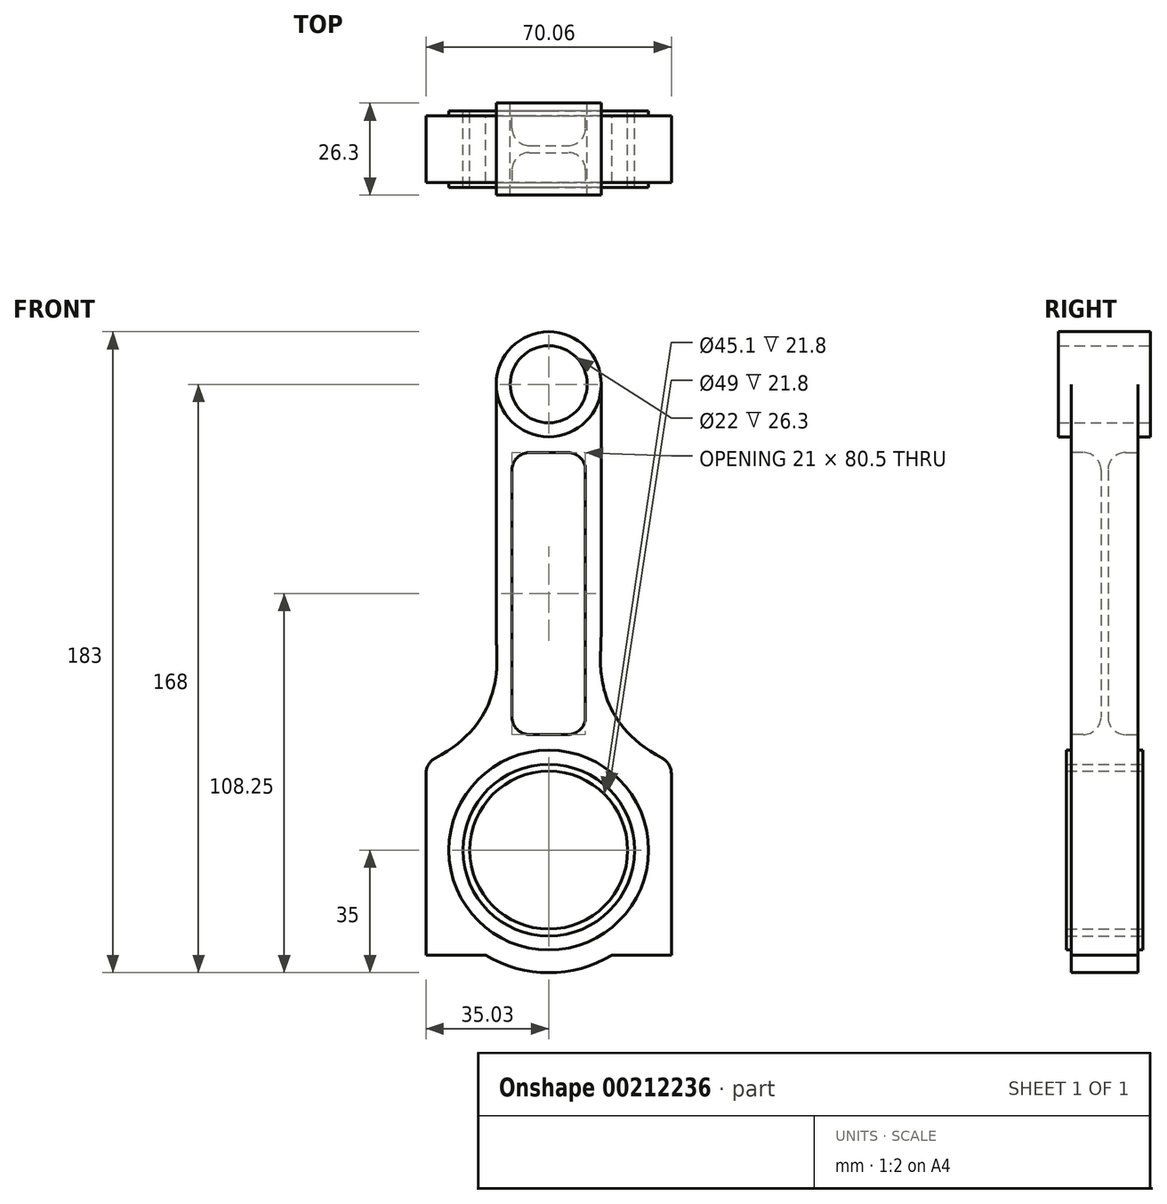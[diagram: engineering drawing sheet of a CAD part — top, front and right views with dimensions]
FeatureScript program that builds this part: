
annotation { "Feature Type Name" : "Feature", "Feature Type Description" : "" }
export const myFeature = defineFeature(function(context is Context, id is Id, definition is map)
    precondition{}
    {
        {
            var Q0;
            Q0=qCreatedBy(makeId("Front.planeOp"),FACE);
            var sketch = newSketch(context, id + "F0", { "sketchPlane" : qUnion([Q0])});
            skCircle(sketch, "E0", {"center": v(0, 0) * mm, "radius": 24.5 * mm});
            skCircle(sketch, "E1", {"center": v(0, 0) * mm, "radius": 22.55 * mm});
            skCircle(sketch, "E2", {"center": v(0, 133) * mm, "radius": 11 * mm});
            skCircle(sketch, "E3", {"center": v(0, 0) * mm, "radius": 28.5 * mm});
            skCircle(sketch, "E4", {"center": v(0, 133) * mm, "radius": 15 * mm});
            skLineSegment(sketch, "E5", {"start": v(0, 172.33) * mm, "end": v(0, -46.15) * mm, "construction": true});
            skCircle(sketch, "E6", {"center": v(0, 0) * mm, "radius": 35 * mm});
            skLineSegment(sketch, "E7", {"start": v(55.37, 133) * mm, "end": v(-76.38, 133) * mm, "construction": true});
            skLineSegment(sketch, "E8", {"start": v(-15, 133) * mm, "end": v(-15, 31.62) * mm});
            skLineSegment(sketch, "E9.MirrorCS", {"start": v(15, 133) * mm, "end": v(15, 31.62) * mm});
            skFitSpline(sketch, "E10", {"points": [v(-15, 65) * mm, v(-15, 50.33) * mm, v(-35.03, 25) * mm], "startDerivative": vector(0, -61.56) * mm, "endDerivative": vector(-82.01, -36.74) * mm});
            skLineSegment(sketch, "E11", {"start": v(-35.03, 25) * mm, "end": v(-35.03, -30) * mm});
            skLineSegment(sketch, "E12", {"start": v(-35.03, -30) * mm, "end": v(-18.03, -30) * mm});
            skFitSpline(sketch, "E13.MirrorCS", {"points": [v(15, 65) * mm, v(15, 50.33) * mm, v(35.03, 25) * mm], "startDerivative": vector(0, -61.56) * mm, "endDerivative": vector(82.01, -36.74) * mm});
            skLineSegment(sketch, "E14.MirrorCS", {"start": v(35.03, 25) * mm, "end": v(35.03, -30) * mm});
            skLineSegment(sketch, "E15.MirrorCS", {"start": v(35.03, -30) * mm, "end": v(18.03, -30) * mm});
            skSolve(sketch);
        }
        {
            var Q0;
            {var subQ0=sQuery(id+"F0.wireOp",EDGE,"E10");Q0=makeQuery(id+"F0.imprint","IMPRINT",FACE,{"disambiguationData":[TD([[makeQuery(id+"F0.imprint","IMPRINT",EDGE,{"derivedFrom":subQ0}),1.0]])]});}
            var Q1;
            {var subQ0=sQuery(id+"F0.wireOp",EDGE,"E13.MirrorCS");Q1=makeQuery(id+"F0.imprint","IMPRINT",FACE,{"disambiguationData":[TD([[makeQuery(id+"F0.imprint","IMPRINT",EDGE,{"derivedFrom":subQ0}),-1.0]])]});}
            var Q2;
            Q2=makeQuery(id+"F0.imprint","IMPRINT",FACE,{"disambiguationData":[TD([[makeQuery(id+"F0.imprint","IMPRINT",EDGE,{"derivedFrom":sQuery(id+"F0.wireOp",EDGE,"E3")}),-1.0]])]});
            var Q3;
            {var subQ0=sQuery(id+"F0.wireOp",EDGE,"E8");var subQ4=sQuery(id+"F0.wireOp",EDGE,"E4");var subQ5=makeQuery(id+"F0.imprint","INTERSECT",VERTEX,{"derivedFrom":[subQ4,subQ0]});Q3=makeQuery(id+"F0.imprint","IMPRINT",FACE,{"disambiguationData":[TD([[makeQuery(id+"F0.imprint","IMPRINT",EDGE,{"disambiguationData":[TD([[subQ5,-1.0]])],"derivedFrom":subQ4}),-1.0]])]});}
            extrude(context, id + "F1", {"entities" : qUnion([Q0, Q1, Q2, Q3]), "endBound" : BoundingType.SYMMETRIC, "depth" : 19 * mm});
        }
        {
            var Q0;
            Q0=makeQuery(id+"F0.imprint","IMPRINT",FACE,{"disambiguationData":[TD([[makeQuery(id+"F0.imprint","IMPRINT",EDGE,{"derivedFrom":sQuery(id+"F0.wireOp",EDGE,"E0")}),-1.0]])]});
            extrude(context, id + "F2", {"entities" : qUnion([Q0]), "operationType" : NewBodyOperationType.ADD, "endBound" : BoundingType.SYMMETRIC, "depth" : 21.8 * mm});
        }
        {
            var Q0;
            Q0=makeQuery(id+"F0.imprint","IMPRINT",FACE,{"disambiguationData":[TD([[makeQuery(id+"F0.imprint","IMPRINT",EDGE,{"derivedFrom":sQuery(id+"F0.wireOp",EDGE,"E2")}),-1.0]])]});
            extrude(context, id + "F3", {"entities" : qUnion([Q0]), "operationType" : NewBodyOperationType.ADD, "endBound" : BoundingType.SYMMETRIC, "depth" : 26.3 * mm});
        }
        {
            var Q0;
            Q0=makeQuery(id+"F0.imprint","IMPRINT",FACE,{"disambiguationData":[TD([[makeQuery(id+"F0.imprint","IMPRINT",EDGE,{"derivedFrom":sQuery(id+"F0.wireOp",EDGE,"E0")}),1.0]])]});
            extrude(context, id + "F4", {"entities" : qUnion([Q0]), "endBound" : BoundingType.SYMMETRIC, "depth" : 21.8 * mm});
        }
        {
            var Q0;
            Q0=makeQuery(id+"F1.opExtrude","CAP_FACE",FACE,{"disambiguationData":[OSD([sQuery(id+"F0.wireOp",EDGE,"E3"),sQuery(id+"F0.wireOp",EDGE,"E4"),sQuery(id+"F0.wireOp",EDGE,"E6"),sQuery(id+"F0.wireOp",EDGE,"E8"),sQuery(id+"F0.wireOp",EDGE,"E9.MirrorCS"),sQuery(id+"F0.wireOp",EDGE,"E10"),sQuery(id+"F0.wireOp",EDGE,"E11"),sQuery(id+"F0.wireOp",EDGE,"E12"),sQuery(id+"F0.wireOp",EDGE,"E13.MirrorCS"),sQuery(id+"F0.wireOp",EDGE,"E14.MirrorCS"),sQuery(id+"F0.wireOp",EDGE,"E15.MirrorCS")])],"isStart":false});
            var sketch = newSketch(context, id + "F5", { "sketchPlane" : qUnion([Q0])});
            skLineSegment(sketch, "E16.bottom", {"start": v(-5.5, 113.5) * mm, "end": v(5.5, 113.5) * mm});
            skLineSegment(sketch, "E16.top", {"start": v(-5.5, 33) * mm, "end": v(5.5, 33) * mm});
            skLineSegment(sketch, "E16.left", {"start": v(-10.5, 108.5) * mm, "end": v(-10.5, 38) * mm});
            skLineSegment(sketch, "E16.right", {"start": v(10.5, 108.5) * mm, "end": v(10.5, 38) * mm});
            skPoint(sketch, "E17.visualSharp", {"position": v(-10.5, 113.5) * mm});
            skArc(sketch, "E17.filletArc", {"start": v(-5.5, 113.5) * mm, "mid": v(-9.04, 112.04) * mm, "end": v(-10.5, 108.5) * mm});
            skPoint(sketch, "E18.visualSharp", {"position": v(10.5, 113.5) * mm});
            skArc(sketch, "E18.filletArc", {"start": v(10.5, 108.5) * mm, "mid": v(9.04, 112.04) * mm, "end": v(5.5, 113.5) * mm});
            skPoint(sketch, "E19.visualSharp", {"position": v(10.5, 33) * mm});
            skArc(sketch, "E19.filletArc", {"start": v(5.5, 33) * mm, "mid": v(9.04, 34.46) * mm, "end": v(10.5, 38) * mm});
            skPoint(sketch, "E20.visualSharp", {"position": v(-10.5, 33) * mm});
            skArc(sketch, "E20.filletArc", {"start": v(-10.5, 38) * mm, "mid": v(-9.04, 34.46) * mm, "end": v(-5.5, 33) * mm});
            skSolve(sketch);
        }
        {
            var Q0;
            Q0 = qSketchRegion(id + "F5", true);
            extrude(context, id + "F6", {"entities" : qUnion([Q0]), "operationType" : NewBodyOperationType.REMOVE, "oppositeDirection" : true, "depth" : (23 / 2 - 3) * mm});
        }
        {
            var Q0;
            Q0=makeQuery(id+"F6.boolean.opBoolean","COPY",EDGE,{"derivedFrom":makeQuery(id+"F6.opExtrude","CAP_EDGE",EDGE,{"disambiguationData":[OSD([sQuery(id+"F5.wireOp",EDGE,"E16.right")])],"isStart":false})});
            var Q1;
            Q1=makeQuery(id+"F6.boolean.opBoolean","COPY",EDGE,{"derivedFrom":makeQuery(id+"F6.opExtrude","CAP_EDGE",EDGE,{"disambiguationData":[OSD([sQuery(id+"F5.wireOp",EDGE,"E16.bottom")])],"isStart":false})});
            var Q2;
            Q2=makeQuery(id+"F6.boolean.opBoolean","COPY",EDGE,{"derivedFrom":makeQuery(id+"F6.opExtrude","CAP_EDGE",EDGE,{"disambiguationData":[OSD([sQuery(id+"F5.wireOp",EDGE,"E18.filletArc")])],"isStart":false})});
            var Q3;
            Q3=makeQuery(id+"F6.boolean.opBoolean","COPY",FACE,{"derivedFrom":makeQuery(id+"F6.opExtrude","CAP_FACE",FACE,{"disambiguationData":[OSD([sQuery(id+"F5.wireOp",EDGE,"E16.bottom"),sQuery(id+"F5.wireOp",EDGE,"E16.top"),sQuery(id+"F5.wireOp",EDGE,"E16.left"),sQuery(id+"F5.wireOp",EDGE,"E16.right"),sQuery(id+"F5.wireOp",EDGE,"E17.filletArc"),sQuery(id+"F5.wireOp",EDGE,"E18.filletArc"),sQuery(id+"F5.wireOp",EDGE,"E19.filletArc"),sQuery(id+"F5.wireOp",EDGE,"E20.filletArc")])],"isStart":false})});
            fillet(context, id + "F7", {"entities" : qUnion([Q0, Q1, Q2, Q3]), "radius" : 5 * mm, "tangentPropagation" : true, "allowEdgeOverflow" : false});
        }
        {
            var Q0;
            Q0=makeQuery(id+"F6.boolean.opBoolean","COPY",FACE,{"derivedFrom":makeQuery(id+"F6.opExtrude","CAP_FACE",FACE,{"disambiguationData":[OSD([sQuery(id+"F5.wireOp",EDGE,"E16.bottom"),sQuery(id+"F5.wireOp",EDGE,"E16.top"),sQuery(id+"F5.wireOp",EDGE,"E16.left"),sQuery(id+"F5.wireOp",EDGE,"E16.right"),sQuery(id+"F5.wireOp",EDGE,"E17.filletArc"),sQuery(id+"F5.wireOp",EDGE,"E18.filletArc"),sQuery(id+"F5.wireOp",EDGE,"E19.filletArc"),sQuery(id+"F5.wireOp",EDGE,"E20.filletArc")])],"isStart":false})});
            var Q1;
            Q1=makeQuery(id+"F7.opFillet","BLEND_FACE",FACE,{"disambiguationData":[OSD([sQuery(id+"F5.wireOp",EDGE,"E16.left")])]});
            var Q2;
            Q2=makeQuery(id+"F6.boolean.opBoolean","COPY",FACE,{"derivedFrom":makeQuery(id+"F6.opExtrude","SWEPT_FACE",FACE,{"disambiguationData":[OSD([sQuery(id+"F5.wireOp",EDGE,"E16.left")])]})});
            var Q3;
            Q3=makeQuery(id+"F7.opFillet","BLEND_FACE",FACE,{"disambiguationData":[OSD([sQuery(id+"F5.wireOp",EDGE,"E20.filletArc")])]});
            var Q4;
            Q4=makeQuery(id+"F6.boolean.opBoolean","COPY",FACE,{"derivedFrom":makeQuery(id+"F6.opExtrude","SWEPT_FACE",FACE,{"disambiguationData":[OSD([sQuery(id+"F5.wireOp",EDGE,"E20.filletArc")])]})});
            var Q5;
            Q5=makeQuery(id+"F6.boolean.opBoolean","COPY",FACE,{"derivedFrom":makeQuery(id+"F6.opExtrude","SWEPT_FACE",FACE,{"disambiguationData":[OSD([sQuery(id+"F5.wireOp",EDGE,"E16.top")])]})});
            var Q6;
            Q6=makeQuery(id+"F7.opFillet","BLEND_FACE",FACE,{"disambiguationData":[OSD([sQuery(id+"F5.wireOp",EDGE,"E16.top")])]});
            var Q7;
            Q7=makeQuery(id+"F7.opFillet","BLEND_FACE",FACE,{"disambiguationData":[OSD([sQuery(id+"F5.wireOp",EDGE,"E19.filletArc")])]});
            var Q8;
            Q8=makeQuery(id+"F6.boolean.opBoolean","COPY",FACE,{"derivedFrom":makeQuery(id+"F6.opExtrude","SWEPT_FACE",FACE,{"disambiguationData":[OSD([sQuery(id+"F5.wireOp",EDGE,"E19.filletArc")])]})});
            var Q9;
            Q9=makeQuery(id+"F7.opFillet","BLEND_FACE",FACE,{"disambiguationData":[OSD([sQuery(id+"F5.wireOp",EDGE,"E16.right")])]});
            var Q10;
            Q10=makeQuery(id+"F6.boolean.opBoolean","COPY",FACE,{"derivedFrom":makeQuery(id+"F6.opExtrude","SWEPT_FACE",FACE,{"disambiguationData":[OSD([sQuery(id+"F5.wireOp",EDGE,"E16.right")])]})});
            var Q11;
            Q11=makeQuery(id+"F7.opFillet","BLEND_FACE",FACE,{"disambiguationData":[OSD([sQuery(id+"F5.wireOp",EDGE,"E18.filletArc")])]});
            var Q12;
            Q12=makeQuery(id+"F6.boolean.opBoolean","COPY",FACE,{"derivedFrom":makeQuery(id+"F6.opExtrude","SWEPT_FACE",FACE,{"disambiguationData":[OSD([sQuery(id+"F5.wireOp",EDGE,"E18.filletArc")])]})});
            var Q13;
            Q13=makeQuery(id+"F6.boolean.opBoolean","COPY",FACE,{"derivedFrom":makeQuery(id+"F6.opExtrude","SWEPT_FACE",FACE,{"disambiguationData":[OSD([sQuery(id+"F5.wireOp",EDGE,"E16.bottom")])]})});
            var Q14;
            Q14=makeQuery(id+"F7.opFillet","BLEND_FACE",FACE,{"disambiguationData":[OSD([sQuery(id+"F5.wireOp",EDGE,"E16.bottom")])]});
            var Q15;
            Q15=makeQuery(id+"F7.opFillet","BLEND_FACE",FACE,{"disambiguationData":[OSD([sQuery(id+"F5.wireOp",EDGE,"E17.filletArc")])]});
            var Q16;
            Q16=makeQuery(id+"F6.boolean.opBoolean","COPY",FACE,{"derivedFrom":makeQuery(id+"F6.opExtrude","SWEPT_FACE",FACE,{"disambiguationData":[OSD([sQuery(id+"F5.wireOp",EDGE,"E17.filletArc")])]})});
            var Q17;
            Q17=qCreatedBy(makeId("Front.planeOp"),FACE);
            mirror(context, id + "F8", {"patternType" : MirrorType.FACE, "faces" : qUnion([Q0, Q1, Q2, Q3, Q4, Q5, Q6, Q7, Q8, Q9, Q10, Q11, Q12, Q13, Q14, Q15, Q16]), "mirrorPlane" : qUnion([Q17])});
        }
        {
            var Q0;
            Q0=makeQuery(id+"F1.opExtrude","SWEPT_EDGE",EDGE,{"disambiguationData":[OSD([sQuery(id+"F0.wireOp",EDGE,"E13.MirrorCS"),sQuery(id+"F0.wireOp",EDGE,"E14.MirrorCS")])]});
            var Q1;
            Q1=makeQuery(id+"F1.opExtrude","SWEPT_EDGE",EDGE,{"disambiguationData":[OSD([sQuery(id+"F0.wireOp",EDGE,"E10"),sQuery(id+"F0.wireOp",EDGE,"E11")])]});
            fillet(context, id + "F9", {"entities" : qUnion([Q0, Q1]), "radius" : 5 * mm, "tangentPropagation" : true, "allowEdgeOverflow" : false});
        }
    });
